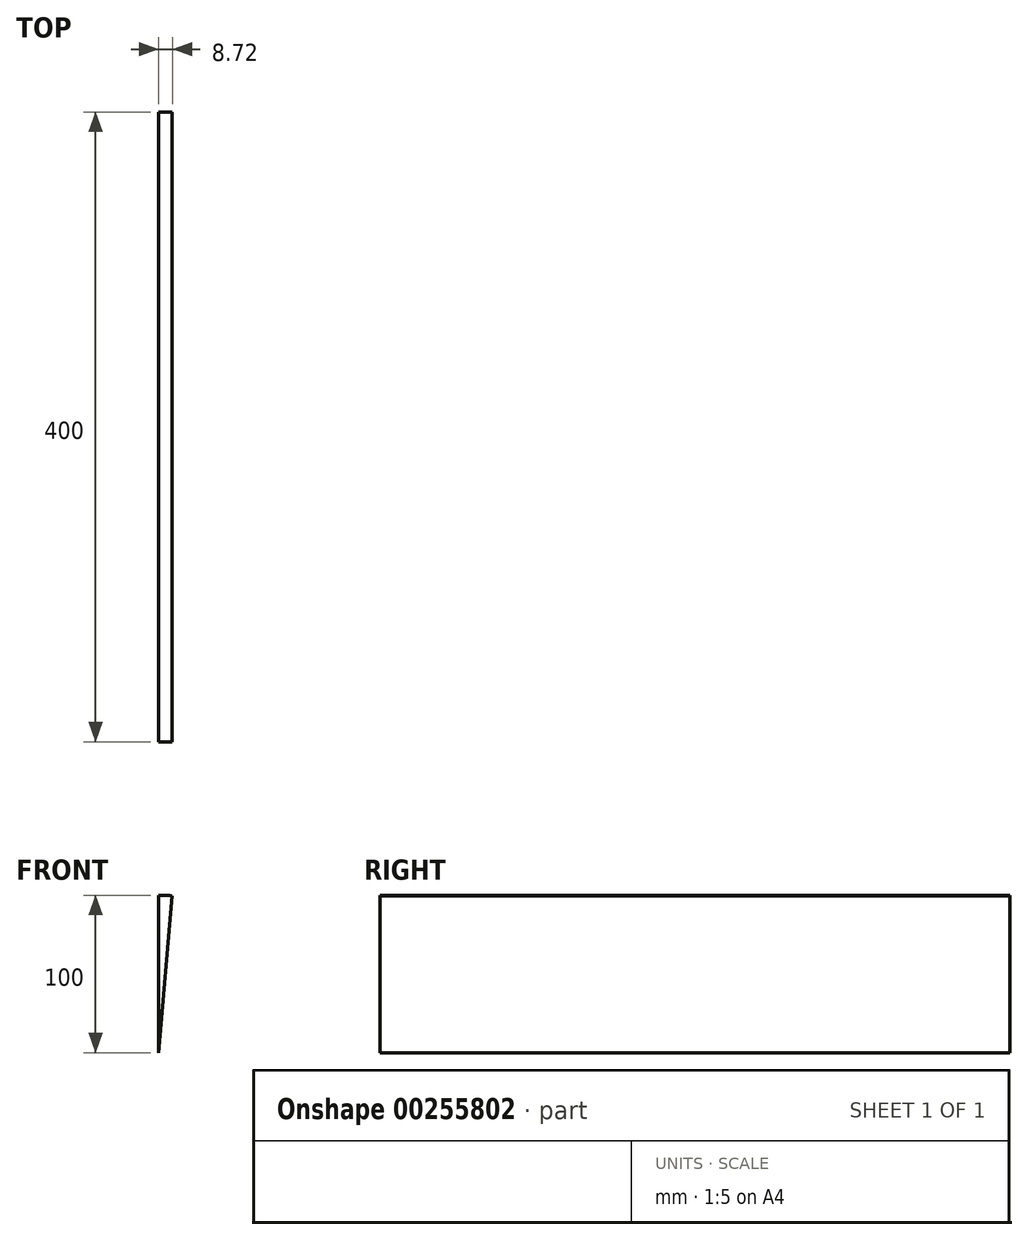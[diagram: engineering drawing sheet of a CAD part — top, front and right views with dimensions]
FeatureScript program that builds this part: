
annotation { "Feature Type Name" : "Feature", "Feature Type Description" : "" }
export const myFeature = defineFeature(function(context is Context, id is Id, definition is map)
    precondition{}
    {
        {
            var Q0;
            Q0=qCreatedBy(makeId("Front.planeOp"),FACE);
            var sketch = newSketch(context, id + "F0", { "sketchPlane" : qUnion([Q0])});
            skCircle(sketch, "E0", {"center": v(0, 0) * mm, "radius": 100 * mm});
            skLineSegment(sketch, "E1", {"start": v(0, 0) * mm, "end": v(0, 100) * mm});
            skLineSegment(sketch, "E2", {"start": v(0, 0) * mm, "end": v(8.72, 99.62) * mm});
            skSolve(sketch);
        }
        {
            var Q0;
            {var subQ0=sQuery(id+"F0.wireOp",EDGE,"E1");Q0=makeQuery(id+"F0.imprint","IMPRINT",FACE,{"disambiguationData":[TD([[makeQuery(id+"F0.imprint","IMPRINT",EDGE,{"derivedFrom":subQ0}),-1.0]])]});}
            extrude(context, id + "F1", {"entities" : qUnion([Q0]), "oppositeDirection" : true, "depth" : 400 * mm});
        }
    });
